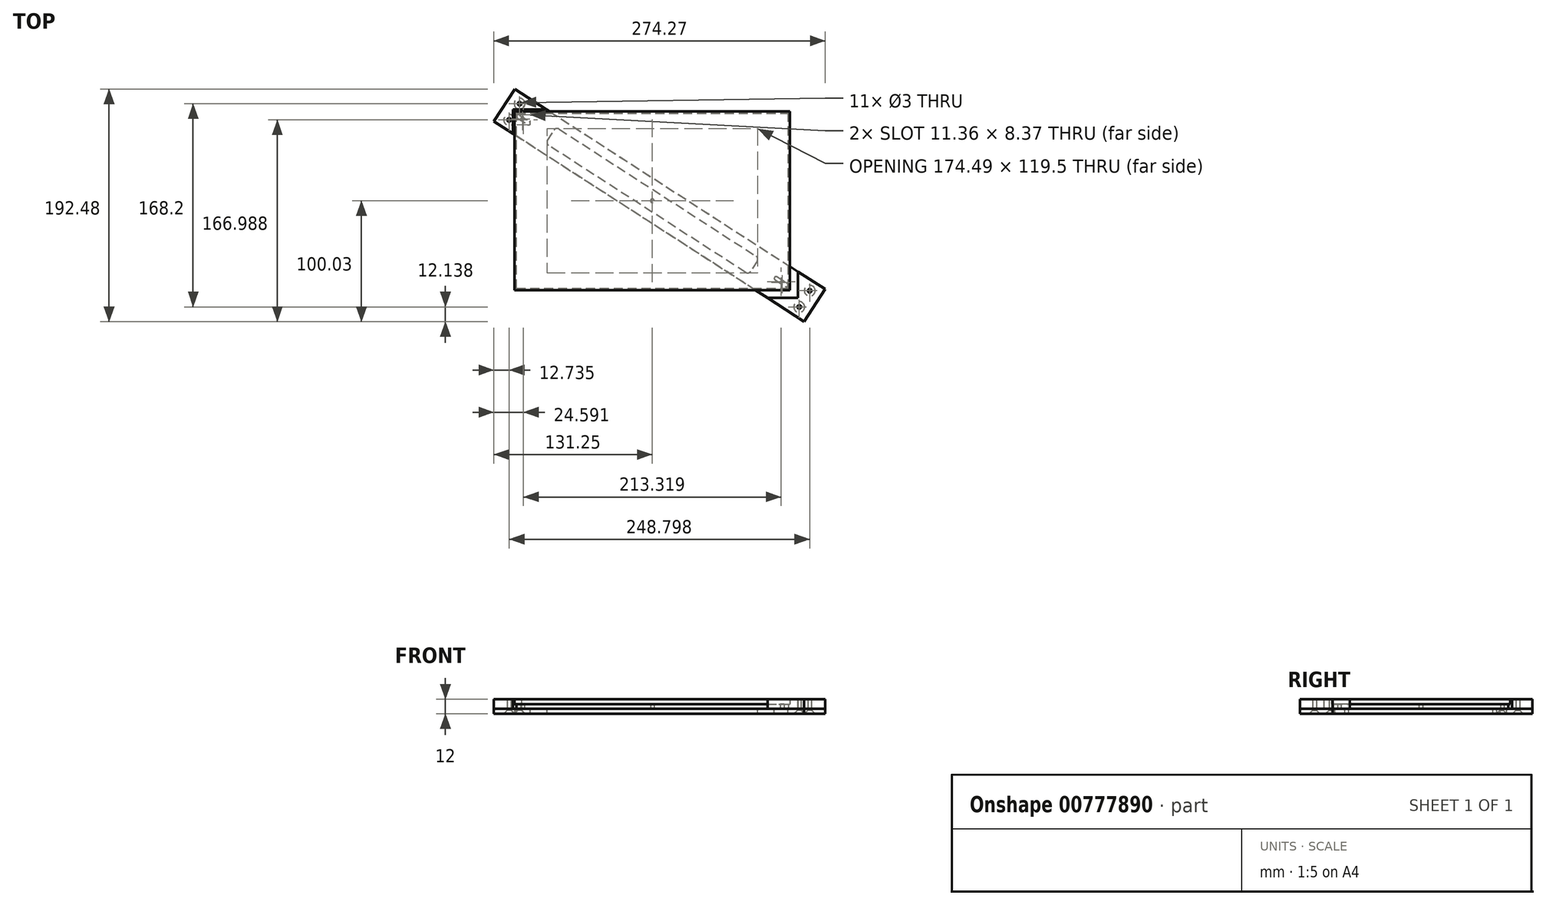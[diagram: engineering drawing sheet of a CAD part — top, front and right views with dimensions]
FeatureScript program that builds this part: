
annotation { "Feature Type Name" : "Feature", "Feature Type Description" : "" }
export const myFeature = defineFeature(function(context is Context, id is Id, definition is map)
    precondition{}
    {
        {
            assignVariable(context, id + "F0", {"name" : "printPlateThickness", "anyValue" : 4 * mm});
        }
        {
            var Q0;
            Q0=qCreatedBy(makeId("Top.planeOp"),FACE);
            var sketch = newSketch(context, id + "F1", { "sketchPlane" : qUnion([Q0])});
            skLineSegment(sketch, "E0.bottom", {"start": v(0, 0) * mm, "end": v(225, 0) * mm});
            skLineSegment(sketch, "E0.top", {"start": v(0, 145) * mm, "end": v(225, 145) * mm});
            skLineSegment(sketch, "E0.left", {"start": v(0, 0) * mm, "end": v(0, 145) * mm});
            skLineSegment(sketch, "E0.right", {"start": v(225, 0) * mm, "end": v(225, 145) * mm});
            skCircle(sketch, "E1", {"center": v(5, 140) * mm, "radius": 1.5 * mm});
            skCircle(sketch, "E2", {"center": v(220, 5) * mm, "radius": 1.5 * mm});
            skLineSegment(sketch, "E3.bottom", {"start": v(-1.5, 146.5) * mm, "end": v(226.5, 146.5) * mm});
            skLineSegment(sketch, "E3.top", {"start": v(-1.5, -1.5) * mm, "end": v(226.5, -1.5) * mm});
            skLineSegment(sketch, "E3.left", {"start": v(-1.5, 146.5) * mm, "end": v(-1.5, -1.5) * mm});
            skLineSegment(sketch, "E3.right", {"start": v(226.5, 146.5) * mm, "end": v(226.5, -1.5) * mm});
            skLineSegment(sketch, "E4", {"start": v(0, 0) * mm, "end": v(225, 145) * mm, "construction": true});
            skLineSegment(sketch, "E5", {"start": v(0, 145) * mm, "end": v(225, 0) * mm, "construction": true});
            skCircle(sketch, "E6", {"center": v(112.5, 72.5) * mm, "radius": 1.5 * mm});
            skSolve(sketch);
        }
        {
            var Q0;
            Q0=makeQuery(id+"F1.imprint","IMPRINT",FACE,{"disambiguationData":[TD([[makeQuery(id+"F1.imprint","IMPRINT",EDGE,{"derivedFrom":sQuery(id+"F1.wireOp",EDGE,"E0.bottom")}),1.0]])]});
            extrude(context, id + "F2", {"entities" : qUnion([Q0]), "depth" : getVariable(context, 'printPlateThickness'), "offsetDistance" : 25 * mm});
        }
        {
            var Q0;
            Q0=qCreatedBy(makeId("Top.planeOp"),FACE);
            var sketch = newSketch(context, id + "F3", { "sketchPlane" : qUnion([Q0])});
            skLineSegment(sketch, "E7", {"start": v(0, 145) * mm, "end": v(225, 0) * mm, "construction": true});
            skLineSegment(sketch, "E8", {"start": v(225, 0) * mm, "end": v(246.85, -14.08) * mm, "construction": true});
            skLineSegment(sketch, "E9", {"start": v(0, 145) * mm, "end": v(-10.09, 151.5) * mm, "construction": true});
            skLineSegment(sketch, "E10", {"start": v(-18.75, 138.05) * mm, "end": v(-1.42, 164.95) * mm});
            skLineSegment(sketch, "E11", {"start": v(-1.42, 164.95) * mm, "end": v(255.52, -0.64) * mm});
            skLineSegment(sketch, "E12", {"start": v(255.52, -0.64) * mm, "end": v(238.19, -27.53) * mm});
            skLineSegment(sketch, "E13", {"start": v(238.19, -27.53) * mm, "end": v(-18.75, 138.05) * mm});
            skCircle(sketch, "E14", {"center": v(2.65, 152.8) * mm, "radius": 1.5 * mm});
            skCircle(sketch, "E15", {"center": v(-6.01, 139.36) * mm, "radius": 1.5 * mm});
            skCircle(sketch, "E16", {"center": v(234.12, -15.4) * mm, "radius": 1.5 * mm});
            skCircle(sketch, "E17", {"center": v(242.78, -1.94) * mm, "radius": 1.5 * mm});
            skLineSegment(sketch, "E18", {"start": v(5, 140) * mm, "end": v(45.54, 113.87) * mm, "construction": true});
            skLineSegment(sketch, "E19", {"start": v(175.06, 33.96) * mm, "end": v(220, 5) * mm, "construction": true});
            skLineSegment(sketch, "E20", {"start": v(220, 5) * mm, "end": v(229, -0.8) * mm, "construction": true});
            skLineSegment(sketch, "E21", {"start": v(5, 140) * mm, "end": v(-2.8, 145.03) * mm, "construction": true});
            skLineSegment(sketch, "E22", {"start": v(-1.9, 136.66) * mm, "end": v(3.2, 144.58) * mm, "construction": true});
            skLineSegment(sketch, "E23", {"start": v(11.96, 139.72) * mm, "end": v(6.4, 131.1) * mm, "construction": true});
            skCircle(sketch, "E24", {"center": v(1.64, 142.17) * mm, "radius": 1.5 * mm});
            skCircle(sketch, "E25", {"center": v(10.04, 136.75) * mm, "radius": 1.5 * mm});
            skLineSegment(sketch, "E26", {"start": v(2.45, 143.43) * mm, "end": v(10.86, 138.01) * mm});
            skLineSegment(sketch, "E27", {"start": v(0.83, 140.9) * mm, "end": v(9.23, 135.49) * mm});
            skLineSegment(sketch, "E28", {"start": v(217.61, 12.37) * mm, "end": v(212.26, 4.07) * mm, "construction": true});
            skLineSegment(sketch, "E29", {"start": v(226.04, 6.99) * mm, "end": v(221.04, -0.77) * mm, "construction": true});
            skCircle(sketch, "E30", {"center": v(214.96, 8.25) * mm, "radius": 1.5 * mm});
            skCircle(sketch, "E31", {"center": v(223.36, 2.83) * mm, "radius": 1.5 * mm});
            skLineSegment(sketch, "E32", {"start": v(215.77, 9.51) * mm, "end": v(224.17, 4.1) * mm});
            skLineSegment(sketch, "E33", {"start": v(214.14, 6.99) * mm, "end": v(222.55, 1.57) * mm});
            skLineSegment(sketch, "E34", {"start": v(35.3, 131.77) * mm, "end": v(198.37, 26.68) * mm});
            skLineSegment(sketch, "E35", {"start": v(199.27, 22.53) * mm, "end": v(193.85, 14.13) * mm});
            skLineSegment(sketch, "E36", {"start": v(189.7, 13.23) * mm, "end": v(26.63, 118.32) * mm});
            skLineSegment(sketch, "E37", {"start": v(25.73, 122.47) * mm, "end": v(31.15, 130.87) * mm});
            skPoint(sketch, "E38.visualSharp", {"position": v(32.78, 133.4) * mm});
            skArc(sketch, "E38.filletArc", {"start": v(35.3, 131.77) * mm, "mid": v(33.04, 132.18) * mm, "end": v(31.15, 130.87) * mm});
            skPoint(sketch, "E39.visualSharp", {"position": v(24.1, 119.95) * mm});
            skArc(sketch, "E39.filletArc", {"start": v(25.73, 122.47) * mm, "mid": v(25.32, 120.2) * mm, "end": v(26.63, 118.32) * mm});
            skPoint(sketch, "E40.visualSharp", {"position": v(192.22, 11.6) * mm});
            skArc(sketch, "E40.filletArc", {"start": v(189.7, 13.23) * mm, "mid": v(191.96, 12.82) * mm, "end": v(193.85, 14.13) * mm});
            skPoint(sketch, "E41.visualSharp", {"position": v(200.9, 25.05) * mm});
            skArc(sketch, "E41.filletArc", {"start": v(199.27, 22.53) * mm, "mid": v(199.68, 24.8) * mm, "end": v(198.37, 26.68) * mm});
            skLineSegment(sketch, "E42", {"start": v(-1.42, 164.95) * mm, "end": v(7.85, 179.34) * mm});
            skLineSegment(sketch, "E43", {"start": v(242.78, -1.94) * mm, "end": v(257.01, 20.14) * mm});
            skLineSegment(sketch, "E44", {"start": v(0.32, 140.12) * mm, "end": v(8.72, 134.7) * mm});
            skPoint(sketch, "E45", {"position": v(4.52, 137.4) * mm});
            skLineSegment(sketch, "E46", {"start": v(213.17, 5.49) * mm, "end": v(221.58, 0.07) * mm});
            skPoint(sketch, "E47", {"position": v(217.38, 2.78) * mm});
            skSolve(sketch);
        }
        {
            var Q0;
            Q0=qSketchRegion(id+"F3",true);
            extrude(context, id + "F4", {"entities" : qUnion([Q0]), "oppositeDirection" : true, "depth" : 4 * mm, "offsetDistance" : 25 * mm});
        }
        {
            var Q0;
            Q0=makeQuery(id+"F4.opExtrude","CAP_FACE",FACE,{"disambiguationData":[OSD([sQuery(id+"F3.wireOp",EDGE,"E10"),sQuery(id+"F3.wireOp",EDGE,"E11"),sQuery(id+"F3.wireOp",EDGE,"E12"),sQuery(id+"F3.wireOp",EDGE,"E13"),sQuery(id+"F3.wireOp",EDGE,"E14"),sQuery(id+"F3.wireOp",EDGE,"E15"),sQuery(id+"F3.wireOp",EDGE,"E16"),sQuery(id+"F3.wireOp",EDGE,"E17"),sQuery(id+"F3.wireOp",EDGE,"E24"),sQuery(id+"F3.wireOp",EDGE,"E25"),sQuery(id+"F3.wireOp",EDGE,"E26"),sQuery(id+"F3.wireOp",EDGE,"E27"),sQuery(id+"F3.wireOp",EDGE,"E30"),sQuery(id+"F3.wireOp",EDGE,"E31"),sQuery(id+"F3.wireOp",EDGE,"E32"),sQuery(id+"F3.wireOp",EDGE,"E33")])],"isStart":true});
            var sketch = newSketch(context, id + "F5", { "sketchPlane" : qUnion([Q0])});
            skLineSegment(sketch, "E48", {"start": v(-1.42, 164.95) * mm, "end": v(24.88, 148) * mm});
            skLineSegment(sketch, "E49", {"start": v(24.88, 148) * mm, "end": v(-3, 148) * mm});
            skLineSegment(sketch, "E50", {"start": v(-3, 148) * mm, "end": v(-3, 127.9) * mm});
            skLineSegment(sketch, "E51", {"start": v(-3, 127.9) * mm, "end": v(-18.75, 138.05) * mm});
            skLineSegment(sketch, "E52", {"start": v(-18.75, 138.05) * mm, "end": v(-1.42, 164.95) * mm});
            skLineSegment(sketch, "E53", {"start": v(233, 13.88) * mm, "end": v(255.52, -0.64) * mm});
            skLineSegment(sketch, "E54", {"start": v(255.52, -0.64) * mm, "end": v(238.19, -27.53) * mm});
            skLineSegment(sketch, "E55", {"start": v(238.19, -27.53) * mm, "end": v(207.88, -8) * mm});
            skLineSegment(sketch, "E56", {"start": v(207.88, -8) * mm, "end": v(233, -8) * mm});
            skLineSegment(sketch, "E57", {"start": v(233, -8) * mm, "end": v(233, 13.88) * mm});
            skCircle(sketch, "E58", {"center": v(242.78, -1.94) * mm, "radius": 1.25 * mm});
            skCircle(sketch, "E59", {"center": v(234.12, -15.4) * mm, "radius": 1.25 * mm});
            skCircle(sketch, "E60", {"center": v(2.65, 152.8) * mm, "radius": 1.25 * mm});
            skCircle(sketch, "E61", {"center": v(-6.01, 139.36) * mm, "radius": 1.25 * mm});
            skLineSegment(sketch, "E62", {"start": v(234.12, -15.4) * mm, "end": v(227.93, -25) * mm, "construction": true});
            skSolve(sketch);
        }
        {
            var Q0;
            Q0=makeQuery(id+"F5.imprint","IMPRINT",FACE,{"disambiguationData":[TD([[makeQuery(id+"F5.imprint","IMPRINT",EDGE,{"derivedFrom":sQuery(id+"F5.wireOp",EDGE,"E48")}),-1.0]])]});
            extrude(context, id + "F6", {"entities" : qUnion([Q0]), "depth" : 8 * mm, "offsetDistance" : 25 * mm});
        }
        {
            var Q0;
            Q0=makeQuery(id+"F5.imprint","IMPRINT",FACE,{"disambiguationData":[TD([[makeQuery(id+"F5.imprint","IMPRINT",EDGE,{"derivedFrom":sQuery(id+"F5.wireOp",EDGE,"E53")}),-1.0]])]});
            extrude(context, id + "F7", {"entities" : qUnion([Q0]), "depth" : 8 * mm, "offsetDistance" : 25 * mm});
        }
        {
            var Q0;
            Q0=makeQuery(id+"F1.imprint","IMPRINT",FACE,{"disambiguationData":[TD([[makeQuery(id+"F1.imprint","IMPRINT",EDGE,{"derivedFrom":sQuery(id+"F1.wireOp",EDGE,"E0.bottom")}),1.0]])]});
            var Q1;
            Q1=makeQuery(id+"F1.imprint","IMPRINT",FACE,{"disambiguationData":[TD([[makeQuery(id+"F1.imprint","IMPRINT",EDGE,{"derivedFrom":sQuery(id+"F1.wireOp",EDGE,"E0.bottom")}),-1.0]])]});
            var Q2;
            Q2=makeQuery(id+"F1.imprint","IMPRINT",FACE,{"disambiguationData":[TD([[makeQuery(id+"F1.imprint","IMPRINT",EDGE,{"derivedFrom":sQuery(id+"F1.wireOp",EDGE,"E1")}),1.0]])]});
            var Q3;
            Q3=makeQuery(id+"F1.imprint","IMPRINT",FACE,{"disambiguationData":[TD([[makeQuery(id+"F1.imprint","IMPRINT",EDGE,{"derivedFrom":sQuery(id+"F1.wireOp",EDGE,"E2")}),1.0]])]});
            var Q4;
            Q4=makeQuery(id+"F1.imprint","IMPRINT",FACE,{"disambiguationData":[TD([[makeQuery(id+"F1.imprint","IMPRINT",EDGE,{"derivedFrom":sQuery(id+"F1.wireOp",EDGE,"E6")}),1.0]])]});
            extrude(context, id + "F8", {"entities" : qUnion([Q0, Q1, Q2, Q3, Q4]), "depth" : 4 * mm + getVariable(context, 'printPlateThickness'), "offsetDistance" : 25 * mm, "hasSecondDirection" : true, "secondDirectionOppositeDirection" : false, "secondDirectionDepth" : getVariable(context, 'printPlateThickness')});
        }
        {
            var Q0;
            Q0=makeQuery(id+"F4.opExtrude","CAP_EDGE",EDGE,{"disambiguationData":[OSD([sQuery(id+"F3.wireOp",EDGE,"E16")])],"isStart":false});
            var Q1;
            Q1=makeQuery(id+"F4.opExtrude","CAP_EDGE",EDGE,{"disambiguationData":[OSD([sQuery(id+"F3.wireOp",EDGE,"E17")])],"isStart":false});
            var Q2;
            Q2=makeQuery(id+"F4.opExtrude","CAP_EDGE",EDGE,{"disambiguationData":[OSD([sQuery(id+"F3.wireOp",EDGE,"E14")])],"isStart":false});
            var Q3;
            Q3=makeQuery(id+"F4.opExtrude","CAP_EDGE",EDGE,{"disambiguationData":[OSD([sQuery(id+"F3.wireOp",EDGE,"E15")])],"isStart":false});
            chamfer(context, id + "F9", {"entities" : qUnion([Q0, Q1, Q2, Q3]), "width" : 3 * mm, "tangentPropagation" : true});
        }
    });
